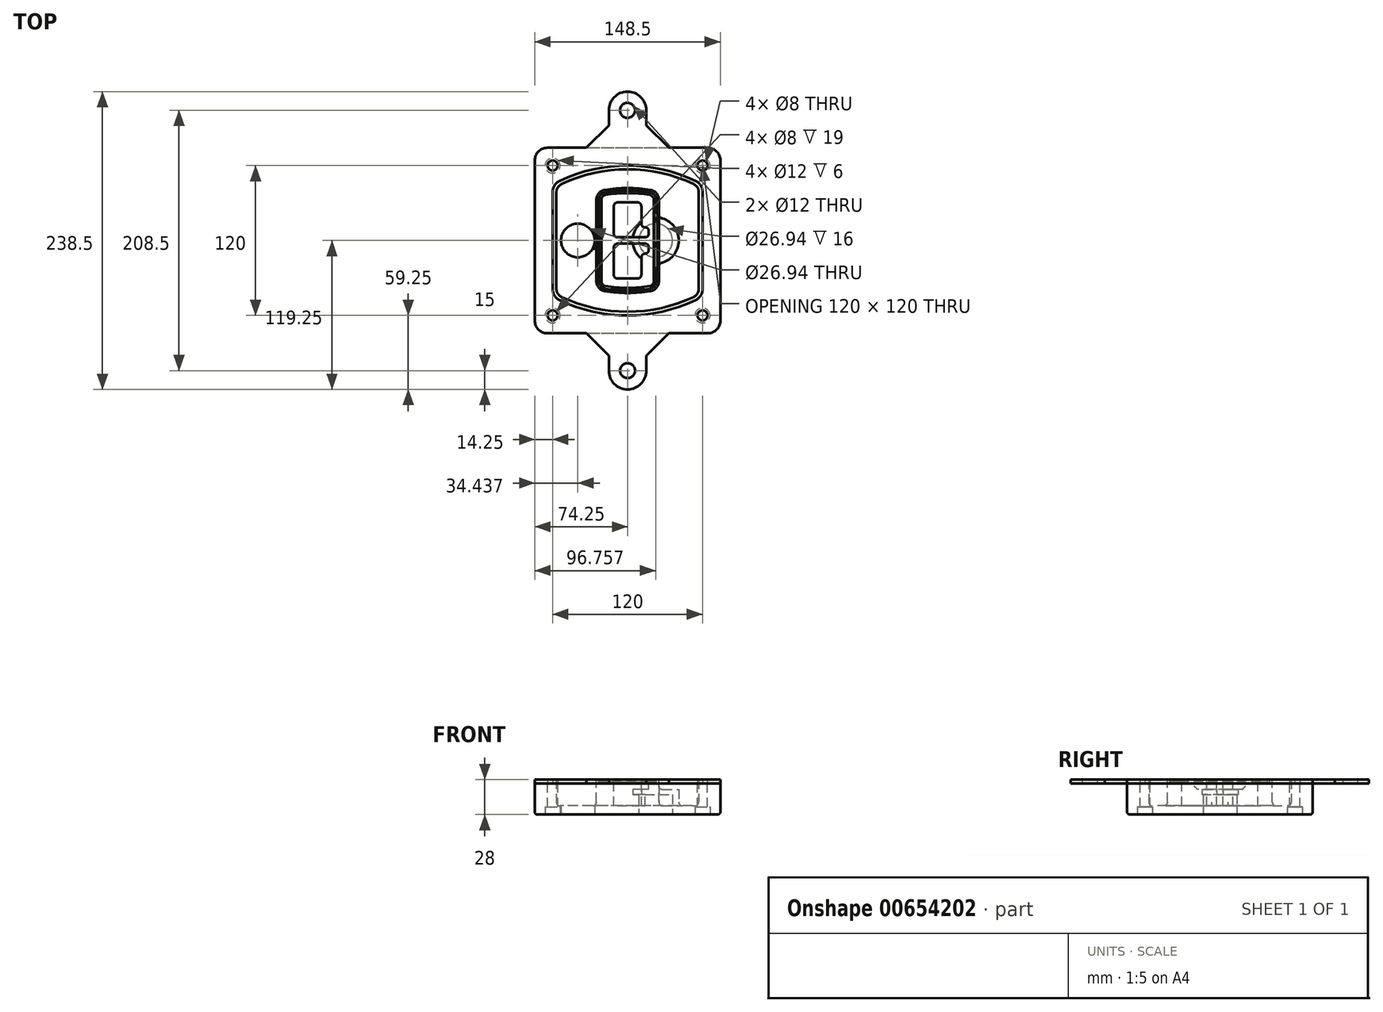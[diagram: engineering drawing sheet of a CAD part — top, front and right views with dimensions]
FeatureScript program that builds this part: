
annotation { "Feature Type Name" : "Feature", "Feature Type Description" : "" }
export const myFeature = defineFeature(function(context is Context, id is Id, definition is map)
    precondition{}
    {
        {
            var Q0;
            Q0=qCreatedBy(makeId("Top.planeOp"),FACE);
            var sketch = newSketch(context, id + "F0", { "sketchPlane" : qUnion([Q0])});
            skPoint(sketch, "E0.rect.middle", {"position": v(0, 0) * mm});
            skLineSegment(sketch, "E1.bottom", {"start": v(-64.25, -74.25) * mm, "end": v(64.25, -74.25) * mm});
            skLineSegment(sketch, "E1.top", {"start": v(-64.25, 74.25) * mm, "end": v(64.25, 74.25) * mm});
            skLineSegment(sketch, "E1.left", {"start": v(-74.25, -64.25) * mm, "end": v(-74.25, 64.25) * mm});
            skLineSegment(sketch, "E1.right", {"start": v(74.25, -64.25) * mm, "end": v(74.25, 64.25) * mm});
            skLineSegment(sketch, "E2", {"start": v(-74.25, 74.25) * mm, "end": v(74.25, -74.25) * mm, "construction": true});
            skLineSegment(sketch, "E3", {"start": v(74.25, 74.25) * mm, "end": v(-74.25, -74.25) * mm, "construction": true});
            skCircle(sketch, "E4", {"center": v(-60, 60) * mm, "radius": 4 * mm});
            skCircle(sketch, "E5", {"center": v(60, 60) * mm, "radius": 4 * mm});
            skCircle(sketch, "E6", {"center": v(60, -60) * mm, "radius": 4 * mm});
            skCircle(sketch, "E7", {"center": v(-60, -60) * mm, "radius": 4 * mm});
            skLineSegment(sketch, "E8", {"start": v(-60, 60) * mm, "end": v(60, 60) * mm, "construction": true});
            skLineSegment(sketch, "E9", {"start": v(60, 60) * mm, "end": v(60, -60) * mm, "construction": true});
            skLineSegment(sketch, "E10", {"start": v(60, -60) * mm, "end": v(-60, -60) * mm, "construction": true});
            skLineSegment(sketch, "E11", {"start": v(-60, -60) * mm, "end": v(-60, 60) * mm, "construction": true});
            skLineSegment(sketch, "E12", {"start": v(-60, 38.83) * mm, "end": v(-60, -38.83) * mm});
            skLineSegment(sketch, "E13", {"start": v(60, 38.83) * mm, "end": v(60, -38.83) * mm});
            skArc(sketch, "E14", {"start": v(54.26, 47.88) * mm, "mid": v(0, 60) * mm, "end": v(-54.26, 47.88) * mm});
            skArc(sketch, "E15", {"start": v(-54.26, -47.88) * mm, "mid": v(0, -60) * mm, "end": v(54.26, -47.88) * mm});
            skLineSegment(sketch, "E16", {"start": v(-60, 0) * mm, "end": v(60, 0) * mm, "construction": true});
            skPoint(sketch, "E17.visualSharp", {"position": v(-60, -45) * mm});
            skArc(sketch, "E17.filletArc", {"start": v(-60, -38.83) * mm, "mid": v(-58.44, -44.2) * mm, "end": v(-54.26, -47.88) * mm});
            skPoint(sketch, "E18.visualSharp", {"position": v(-60, 45) * mm});
            skArc(sketch, "E18.filletArc", {"start": v(-54.26, 47.88) * mm, "mid": v(-58.44, 44.2) * mm, "end": v(-60, 38.83) * mm});
            skPoint(sketch, "E19.visualSharp", {"position": v(60, 45) * mm});
            skArc(sketch, "E19.filletArc", {"start": v(60, 38.83) * mm, "mid": v(58.44, 44.2) * mm, "end": v(54.26, 47.88) * mm});
            skPoint(sketch, "E20.visualSharp", {"position": v(60, -45) * mm});
            skArc(sketch, "E20.filletArc", {"start": v(54.26, -47.88) * mm, "mid": v(58.44, -44.2) * mm, "end": v(60, -38.83) * mm});
            skPoint(sketch, "E21.visualSharp", {"position": v(-74.25, 74.25) * mm});
            skArc(sketch, "E21.filletArc", {"start": v(-64.25, 74.25) * mm, "mid": v(-71.32, 71.32) * mm, "end": v(-74.25, 64.25) * mm});
            skPoint(sketch, "E22.visualSharp", {"position": v(74.25, 74.25) * mm});
            skArc(sketch, "E22.filletArc", {"start": v(74.25, 64.25) * mm, "mid": v(71.32, 71.32) * mm, "end": v(64.25, 74.25) * mm});
            skPoint(sketch, "E23.visualSharp", {"position": v(74.25, -74.25) * mm});
            skArc(sketch, "E23.filletArc", {"start": v(64.25, -74.25) * mm, "mid": v(71.32, -71.32) * mm, "end": v(74.25, -64.25) * mm});
            skPoint(sketch, "E24.visualSharp", {"position": v(-74.25, -74.25) * mm});
            skArc(sketch, "E24.filletArc", {"start": v(-74.25, -64.25) * mm, "mid": v(-71.32, -71.32) * mm, "end": v(-64.25, -74.25) * mm});
            skArc(sketch, "E25.0", {"start": v(57, 38.83) * mm, "mid": v(55.9, 42.58) * mm, "end": v(52.98, 45.17) * mm});
            skLineSegment(sketch, "E25.1", {"start": v(57, 38.83) * mm, "end": v(57, -38.83) * mm});
            skArc(sketch, "E25.2", {"start": v(52.98, -45.17) * mm, "mid": v(55.9, -42.58) * mm, "end": v(57, -38.83) * mm});
            skArc(sketch, "E25.3", {"start": v(-52.98, -45.17) * mm, "mid": v(0, -57) * mm, "end": v(52.98, -45.17) * mm});
            skArc(sketch, "E25.4", {"start": v(-57, -38.83) * mm, "mid": v(-55.9, -42.58) * mm, "end": v(-52.98, -45.17) * mm});
            skArc(sketch, "E25.5", {"start": v(52.98, 45.17) * mm, "mid": v(0, 57) * mm, "end": v(-52.98, 45.17) * mm});
            skLineSegment(sketch, "E25.6", {"start": v(-57, 38.83) * mm, "end": v(-57, -38.83) * mm});
            skArc(sketch, "E25.7", {"start": v(-52.98, 45.17) * mm, "mid": v(-55.9, 42.58) * mm, "end": v(-57, 38.83) * mm});
            skArc(sketch, "E26.0", {"start": v(-55.96, 51.5) * mm, "mid": v(-61.82, 46.33) * mm, "end": v(-64, 38.83) * mm});
            skArc(sketch, "E26.1", {"start": v(55.96, 51.5) * mm, "mid": v(0, 64) * mm, "end": v(-55.96, 51.5) * mm});
            skArc(sketch, "E26.2", {"start": v(64, 38.83) * mm, "mid": v(61.82, 46.33) * mm, "end": v(55.96, 51.5) * mm});
            skLineSegment(sketch, "E26.3", {"start": v(64, 38.83) * mm, "end": v(64, -38.83) * mm});
            skArc(sketch, "E26.4", {"start": v(55.96, -51.5) * mm, "mid": v(61.82, -46.33) * mm, "end": v(64, -38.83) * mm});
            skLineSegment(sketch, "E26.5", {"start": v(-64, 38.83) * mm, "end": v(-64, -38.83) * mm});
            skArc(sketch, "E26.6", {"start": v(-55.96, -51.5) * mm, "mid": v(0, -64) * mm, "end": v(55.96, -51.5) * mm});
            skArc(sketch, "E26.7", {"start": v(-64, -38.83) * mm, "mid": v(-61.82, -46.33) * mm, "end": v(-55.96, -51.5) * mm});
            skSolve(sketch);
        }
        {
            var Q0;
            Q0=makeQuery(id+"F0.imprint","IMPRINT",FACE,{"disambiguationData":[TD([[makeQuery(id+"F0.imprint","IMPRINT",EDGE,{"derivedFrom":sQuery(id+"F0.wireOp",EDGE,"E1.bottom")}),1.0]])]});
            var Q1;
            Q1=makeQuery(id+"F0.imprint","IMPRINT",FACE,{"disambiguationData":[TD([[makeQuery(id+"F0.imprint","IMPRINT",EDGE,{"derivedFrom":sQuery(id+"F0.wireOp",EDGE,"E12")}),1.0]])]});
            var Q2;
            Q2=makeQuery(id+"F0.imprint","IMPRINT",FACE,{"disambiguationData":[TD([[makeQuery(id+"F0.imprint","IMPRINT",EDGE,{"derivedFrom":sQuery(id+"F0.wireOp",EDGE,"E25.0")}),1.0]])]});
            var Q3;
            Q3=makeQuery(id+"F0.imprint","IMPRINT",FACE,{"disambiguationData":[TD([[makeQuery(id+"F0.imprint","IMPRINT",EDGE,{"derivedFrom":sQuery(id+"F0.wireOp",EDGE,"E12")}),-1.0]])]});
            extrude(context, id + "F1", {"entities" : qUnion([Q0, Q1, Q2, Q3]), "oppositeDirection" : true, "depth" : 25 * mm});
        }
        {
            var Q0;
            Q0=makeQuery(id+"F0.imprint","IMPRINT",FACE,{"disambiguationData":[TD([[makeQuery(id+"F0.imprint","IMPRINT",EDGE,{"derivedFrom":sQuery(id+"F0.wireOp",EDGE,"E12")}),1.0]])]});
            extrude(context, id + "F2", {"entities" : qUnion([Q0]), "operationType" : NewBodyOperationType.ADD, "depth" : 3 * mm});
        }
        {
            var Q0;
            Q0=makeQuery(id+"F0.imprint","IMPRINT",FACE,{"disambiguationData":[TD([[makeQuery(id+"F0.imprint","IMPRINT",EDGE,{"derivedFrom":sQuery(id+"F0.wireOp",EDGE,"E25.0")}),1.0]])]});
            extrude(context, id + "F3", {"entities" : qUnion([Q0]), "operationType" : NewBodyOperationType.REMOVE, "oppositeDirection" : true, "depth" : 18 * mm});
        }
        {
            var Q0;
            Q0=makeQuery(id+"F2.opExtrude","CAP_FACE",FACE,{"disambiguationData":[OSD([sQuery(id+"F0.wireOp",EDGE,"E12"),sQuery(id+"F0.wireOp",EDGE,"E13"),sQuery(id+"F0.wireOp",EDGE,"E14"),sQuery(id+"F0.wireOp",EDGE,"E15"),sQuery(id+"F0.wireOp",EDGE,"E17.filletArc"),sQuery(id+"F0.wireOp",EDGE,"E18.filletArc"),sQuery(id+"F0.wireOp",EDGE,"E19.filletArc"),sQuery(id+"F0.wireOp",EDGE,"E20.filletArc"),sQuery(id+"F0.wireOp",EDGE,"E25.0"),sQuery(id+"F0.wireOp",EDGE,"E25.1"),sQuery(id+"F0.wireOp",EDGE,"E25.2"),sQuery(id+"F0.wireOp",EDGE,"E25.3"),sQuery(id+"F0.wireOp",EDGE,"E25.4"),sQuery(id+"F0.wireOp",EDGE,"E25.5"),sQuery(id+"F0.wireOp",EDGE,"E25.6"),sQuery(id+"F0.wireOp",EDGE,"E25.7")])],"isStart":false});
            var sketch = newSketch(context, id + "F4", { "sketchPlane" : qUnion([Q0])});
            skArc(sketch, "E27.0", {"start": v(-18.34, -40.45) * mm, "mid": v(0, -42) * mm, "end": v(18.34, -40.45) * mm});
            skArc(sketch, "E28.0", {"start": v(18.34, 40.45) * mm, "mid": v(0, 42) * mm, "end": v(-18.34, 40.45) * mm});
            skLineSegment(sketch, "E29", {"start": v(-25, 32.57) * mm, "end": v(-25, -32.57) * mm});
            skLineSegment(sketch, "E30", {"start": v(25, 32.57) * mm, "end": v(25, -32.57) * mm});
            skLineSegment(sketch, "E31", {"start": v(-25, 39.1) * mm, "end": v(25, 39.1) * mm, "construction": true});
            skLineSegment(sketch, "E32", {"start": v(-25, -39.1) * mm, "end": v(25, -39.1) * mm, "construction": true});
            skPoint(sketch, "E33.visualSharp", {"position": v(-25, 39.1) * mm});
            skArc(sketch, "E33.filletArc", {"start": v(-18.34, 40.45) * mm, "mid": v(-23.11, 37.73) * mm, "end": v(-25, 32.57) * mm});
            skPoint(sketch, "E34.visualSharp", {"position": v(25, 39.1) * mm});
            skArc(sketch, "E34.filletArc", {"start": v(25, 32.57) * mm, "mid": v(23.11, 37.73) * mm, "end": v(18.34, 40.45) * mm});
            skPoint(sketch, "E35.visualSharp", {"position": v(25, -39.1) * mm});
            skArc(sketch, "E35.filletArc", {"start": v(18.34, -40.45) * mm, "mid": v(23.11, -37.73) * mm, "end": v(25, -32.57) * mm});
            skPoint(sketch, "E36.visualSharp", {"position": v(-25, -39.1) * mm});
            skArc(sketch, "E36.filletArc", {"start": v(-25, -32.57) * mm, "mid": v(-23.11, -37.73) * mm, "end": v(-18.34, -40.45) * mm});
            skArc(sketch, "E37.0", {"start": v(52.98, 45.17) * mm, "mid": v(0, 57) * mm, "end": v(-52.98, 45.17) * mm});
            skArc(sketch, "E37.1", {"start": v(-52.98, 45.17) * mm, "mid": v(-55.9, 42.58) * mm, "end": v(-57, 38.83) * mm});
            skLineSegment(sketch, "E37.2", {"start": v(-57, 38.83) * mm, "end": v(-57, -38.83) * mm});
            skArc(sketch, "E37.3", {"start": v(-57, -38.83) * mm, "mid": v(-55.9, -42.58) * mm, "end": v(-52.98, -45.17) * mm});
            skArc(sketch, "E37.4", {"start": v(-52.98, -45.17) * mm, "mid": v(0, -57) * mm, "end": v(52.98, -45.17) * mm});
            skArc(sketch, "E37.5", {"start": v(52.98, -45.17) * mm, "mid": v(55.9, -42.58) * mm, "end": v(57, -38.83) * mm});
            skLineSegment(sketch, "E37.6", {"start": v(57, 38.83) * mm, "end": v(57, -38.83) * mm});
            skArc(sketch, "E37.7", {"start": v(57, 38.83) * mm, "mid": v(55.9, 42.58) * mm, "end": v(52.98, 45.17) * mm});
            skLineSegment(sketch, "E38.0", {"start": v(23, 32.57) * mm, "end": v(23, -32.57) * mm});
            skArc(sketch, "E38.1", {"start": v(18, -38.48) * mm, "mid": v(21.58, -36.44) * mm, "end": v(23, -32.57) * mm});
            skArc(sketch, "E38.2", {"start": v(-18, -38.48) * mm, "mid": v(0, -40) * mm, "end": v(18, -38.48) * mm});
            skArc(sketch, "E38.3", {"start": v(-23, -32.57) * mm, "mid": v(-21.58, -36.44) * mm, "end": v(-18, -38.48) * mm});
            skLineSegment(sketch, "E38.4", {"start": v(-23, 32.57) * mm, "end": v(-23, -32.57) * mm});
            skArc(sketch, "E38.5", {"start": v(23, 32.57) * mm, "mid": v(21.58, 36.44) * mm, "end": v(18, 38.48) * mm});
            skArc(sketch, "E38.6", {"start": v(-18, 38.48) * mm, "mid": v(-21.58, 36.44) * mm, "end": v(-23, 32.57) * mm});
            skArc(sketch, "E38.7", {"start": v(18, 38.48) * mm, "mid": v(0, 40) * mm, "end": v(-18, 38.48) * mm});
            skArc(sketch, "E39.0", {"start": v(21, 32.57) * mm, "mid": v(20.06, 35.15) * mm, "end": v(17.67, 36.5) * mm});
            skLineSegment(sketch, "E39.1", {"start": v(21, 32.57) * mm, "end": v(21, -32.57) * mm});
            skArc(sketch, "E39.2", {"start": v(17.67, -36.5) * mm, "mid": v(20.06, -35.15) * mm, "end": v(21, -32.57) * mm});
            skArc(sketch, "E39.3", {"start": v(-17.67, -36.5) * mm, "mid": v(0, -38) * mm, "end": v(17.67, -36.5) * mm});
            skArc(sketch, "E39.4", {"start": v(-21, -32.57) * mm, "mid": v(-20.06, -35.15) * mm, "end": v(-17.67, -36.5) * mm});
            skArc(sketch, "E39.5", {"start": v(17.67, 36.5) * mm, "mid": v(0, 38) * mm, "end": v(-17.67, 36.5) * mm});
            skLineSegment(sketch, "E39.6", {"start": v(-21, 32.57) * mm, "end": v(-21, -32.57) * mm});
            skArc(sketch, "E39.7", {"start": v(-17.67, 36.5) * mm, "mid": v(-20.06, 35.15) * mm, "end": v(-21, 32.57) * mm});
            skLineSegment(sketch, "E40", {"start": v(-25, 0) * mm, "end": v(25, 0) * mm, "construction": true});
            skLineSegment(sketch, "E41", {"start": v(-11, 5.5) * mm, "end": v(-11, 27.5) * mm});
            skLineSegment(sketch, "E42", {"start": v(-8, 30.5) * mm, "end": v(8, 30.5) * mm});
            skLineSegment(sketch, "E43", {"start": v(11, 27.5) * mm, "end": v(11, 13.5) * mm});
            skLineSegment(sketch, "E44", {"start": v(14, 10.5) * mm, "end": v(14, 10.5) * mm});
            skLineSegment(sketch, "E45", {"start": v(17, 7.5) * mm, "end": v(17, 5.5) * mm});
            skLineSegment(sketch, "E46", {"start": v(14, 2.5) * mm, "end": v(-8, 2.5) * mm});
            skPoint(sketch, "E47.visualSharp", {"position": v(-11, 30.5) * mm});
            skArc(sketch, "E47.filletArc", {"start": v(-8, 30.5) * mm, "mid": v(-10.12, 29.62) * mm, "end": v(-11, 27.5) * mm});
            skPoint(sketch, "E48.visualSharp", {"position": v(11, 30.5) * mm});
            skArc(sketch, "E48.filletArc", {"start": v(11, 27.5) * mm, "mid": v(10.12, 29.62) * mm, "end": v(8, 30.5) * mm});
            skPoint(sketch, "E49.visualSharp", {"position": v(11, 10.5) * mm});
            skArc(sketch, "E49.filletArc", {"start": v(11, 13.5) * mm, "mid": v(11.88, 11.38) * mm, "end": v(14, 10.5) * mm});
            skPoint(sketch, "E50.visualSharp", {"position": v(17, 10.5) * mm});
            skArc(sketch, "E50.filletArc", {"start": v(17, 7.5) * mm, "mid": v(16.12, 9.62) * mm, "end": v(14, 10.5) * mm});
            skPoint(sketch, "E51.visualSharp", {"position": v(17, 2.5) * mm});
            skArc(sketch, "E51.filletArc", {"start": v(14, 2.5) * mm, "mid": v(16.12, 3.38) * mm, "end": v(17, 5.5) * mm});
            skPoint(sketch, "E52.visualSharp", {"position": v(-11, 2.5) * mm});
            skArc(sketch, "E52.filletArc", {"start": v(-11, 5.5) * mm, "mid": v(-10.12, 3.38) * mm, "end": v(-8, 2.5) * mm});
            skLineSegment(sketch, "E53.0.MirrorCS", {"start": v(14, -2.5) * mm, "end": v(-8, -2.5) * mm});
            skArc(sketch, "E54.0.MirrorCS", {"start": v(-11, -5.5) * mm, "mid": v(-10.12, -3.38) * mm, "end": v(-8, -2.5) * mm});
            skLineSegment(sketch, "E55.0.MirrorCS", {"start": v(-11, -5.5) * mm, "end": v(-11, -27.5) * mm});
            skArc(sketch, "E56.0.MirrorCS", {"start": v(-8, -30.5) * mm, "mid": v(-10.12, -29.62) * mm, "end": v(-11, -27.5) * mm});
            skLineSegment(sketch, "E57.0.MirrorCS", {"start": v(-8, -30.5) * mm, "end": v(8, -30.5) * mm});
            skArc(sketch, "E58.0.MirrorCS", {"start": v(11, -27.5) * mm, "mid": v(10.12, -29.62) * mm, "end": v(8, -30.5) * mm});
            skLineSegment(sketch, "E59.0.MirrorCS", {"start": v(11, -27.5) * mm, "end": v(11, -13.5) * mm});
            skArc(sketch, "E60.0.MirrorCS", {"start": v(11, -13.5) * mm, "mid": v(11.88, -11.38) * mm, "end": v(14, -10.5) * mm});
            skArc(sketch, "E61.0.MirrorCS", {"start": v(17, -7.5) * mm, "mid": v(16.12, -9.62) * mm, "end": v(14, -10.5) * mm});
            skLineSegment(sketch, "E62.0.MirrorCS", {"start": v(17, -7.5) * mm, "end": v(17, -5.5) * mm});
            skArc(sketch, "E63.0.MirrorCS", {"start": v(14, -2.5) * mm, "mid": v(16.12, -3.38) * mm, "end": v(17, -5.5) * mm});
            skSolve(sketch);
        }
        {
            var Q0;
            Q0=makeQuery(id+"F4.imprint","IMPRINT",FACE,{"disambiguationData":[TD([[makeQuery(id+"F4.imprint","IMPRINT",EDGE,{"derivedFrom":sQuery(id+"F4.wireOp",EDGE,"E27.0")}),1.0]])]});
            var Q1;
            Q1=makeQuery(id+"F4.imprint","IMPRINT",FACE,{"disambiguationData":[TD([[makeQuery(id+"F4.imprint","IMPRINT",EDGE,{"derivedFrom":sQuery(id+"F4.wireOp",EDGE,"E38.0")}),-1.0]])]});
            var Q2;
            Q2=makeQuery(id+"F4.imprint","IMPRINT",FACE,{"disambiguationData":[TD([[makeQuery(id+"F4.imprint","IMPRINT",EDGE,{"derivedFrom":sQuery(id+"F4.wireOp",EDGE,"E39.0")}),1.0]])]});
            extrude(context, id + "F5", {"entities" : qUnion([Q0, Q1, Q2]), "operationType" : NewBodyOperationType.ADD, "endBound" : BoundingType.UP_TO_NEXT, "oppositeDirection" : true, "depth" : 25 * mm});
        }
        {
            var Q0;
            Q0=makeQuery(id+"F4.imprint","IMPRINT",FACE,{"disambiguationData":[TD([[makeQuery(id+"F4.imprint","IMPRINT",EDGE,{"derivedFrom":sQuery(id+"F4.wireOp",EDGE,"E38.0")}),-1.0]])]});
            extrude(context, id + "F6", {"entities" : qUnion([Q0]), "operationType" : NewBodyOperationType.REMOVE, "oppositeDirection" : true, "depth" : 2 * mm});
        }
        {
            var Q0;
            Q0=makeQuery(id+"F1.opExtrude","CAP_FACE",FACE,{"disambiguationData":[OSD([sQuery(id+"F0.wireOp",EDGE,"E1.bottom"),sQuery(id+"F0.wireOp",EDGE,"E1.top"),sQuery(id+"F0.wireOp",EDGE,"E1.left"),sQuery(id+"F0.wireOp",EDGE,"E1.right"),sQuery(id+"F0.wireOp",EDGE,"E4"),sQuery(id+"F0.wireOp",EDGE,"E5"),sQuery(id+"F0.wireOp",EDGE,"E6"),sQuery(id+"F0.wireOp",EDGE,"E7"),sQuery(id+"F0.wireOp",EDGE,"E21.filletArc"),sQuery(id+"F0.wireOp",EDGE,"E22.filletArc"),sQuery(id+"F0.wireOp",EDGE,"E23.filletArc"),sQuery(id+"F0.wireOp",EDGE,"E24.filletArc")])],"isStart":false});
            var sketch = newSketch(context, id + "F7", { "sketchPlane" : qUnion([Q0])});
            skCircle(sketch, "E64", {"center": v(22.5, 0) * mm, "radius": 13.47 * mm});
            skCircle(sketch, "E65", {"center": v(-39.81, 0) * mm, "radius": 13.47 * mm});
            skLineSegment(sketch, "E66", {"start": v(74.25, 0) * mm, "end": v(-74.25, 0) * mm});
            skCircle(sketch, "E67", {"center": v(22.5, 0) * mm, "radius": 18.47 * mm});
            skCircle(sketch, "E68", {"center": v(60, -60) * mm, "radius": 6 * mm});
            skCircle(sketch, "E69", {"center": v(-60, -60) * mm, "radius": 6 * mm});
            skCircle(sketch, "E70", {"center": v(-60, 60) * mm, "radius": 6 * mm});
            skCircle(sketch, "E71", {"center": v(60, 60) * mm, "radius": 6 * mm});
            skSolve(sketch);
        }
        {
            var Q0;
            {var subQ1=sQuery(id+"F7.wireOp",EDGE,"E66");var subQ4=sQuery(id+"F7.wireOp",EDGE,"E64");var subQ6=makeQuery(id+"F7.imprint","INTERSECT",VERTEX,{"disambiguationData":[OD(0.0)],"derivedFrom":[subQ4,subQ1]});Q0=makeQuery(id+"F7.imprint","IMPRINT",FACE,{"disambiguationData":[TD([[makeQuery(id+"F7.imprint","IMPRINT",EDGE,{"disambiguationData":[TD([[subQ6,-1.0]])],"derivedFrom":subQ4}),-1.0]])]});}
            var Q1;
            {var subQ0=sQuery(id+"F7.wireOp",EDGE,"E66");var subQ1=sQuery(id+"F7.wireOp",EDGE,"E64");var subQ3=makeQuery(id+"F7.imprint","INTERSECT",VERTEX,{"disambiguationData":[OD(0.0)],"derivedFrom":[subQ1,subQ0]});Q1=makeQuery(id+"F7.imprint","IMPRINT",FACE,{"disambiguationData":[TD([[makeQuery(id+"F7.imprint","IMPRINT",EDGE,{"disambiguationData":[TD([[subQ3,-1.0]])],"derivedFrom":subQ1}),1.0]])]});}
            var Q2;
            {var subQ0=sQuery(id+"F7.wireOp",EDGE,"E66");var subQ1=sQuery(id+"F7.wireOp",EDGE,"E64");var subQ3=makeQuery(id+"F7.imprint","INTERSECT",VERTEX,{"disambiguationData":[OD(0.0)],"derivedFrom":[subQ1,subQ0]});Q2=makeQuery(id+"F7.imprint","IMPRINT",FACE,{"disambiguationData":[TD([[makeQuery(id+"F7.imprint","IMPRINT",EDGE,{"disambiguationData":[TD([[subQ3,1.0]])],"derivedFrom":subQ1}),1.0]])]});}
            var Q3;
            {var subQ1=sQuery(id+"F7.wireOp",EDGE,"E66");var subQ4=sQuery(id+"F7.wireOp",EDGE,"E64");var subQ6=makeQuery(id+"F7.imprint","INTERSECT",VERTEX,{"disambiguationData":[OD(0.0)],"derivedFrom":[subQ4,subQ1]});Q3=makeQuery(id+"F7.imprint","IMPRINT",FACE,{"disambiguationData":[TD([[makeQuery(id+"F7.imprint","IMPRINT",EDGE,{"disambiguationData":[TD([[subQ6,1.0]])],"derivedFrom":subQ4}),-1.0]])]});}
            extrude(context, id + "F8", {"entities" : qUnion([Q0, Q1, Q2, Q3]), "operationType" : NewBodyOperationType.ADD, "oppositeDirection" : true, "depth" : 20 * mm});
        }
        {
            var Q0;
            {var subQ0=sQuery(id+"F7.wireOp",EDGE,"E66");var subQ1=sQuery(id+"F7.wireOp",EDGE,"E64");var subQ3=makeQuery(id+"F7.imprint","INTERSECT",VERTEX,{"disambiguationData":[OD(0.0)],"derivedFrom":[subQ1,subQ0]});Q0=makeQuery(id+"F7.imprint","IMPRINT",FACE,{"disambiguationData":[TD([[makeQuery(id+"F7.imprint","IMPRINT",EDGE,{"disambiguationData":[TD([[subQ3,-1.0]])],"derivedFrom":subQ1}),1.0]])]});}
            var Q1;
            {var subQ0=sQuery(id+"F7.wireOp",EDGE,"E66");var subQ1=sQuery(id+"F7.wireOp",EDGE,"E64");var subQ3=makeQuery(id+"F7.imprint","INTERSECT",VERTEX,{"disambiguationData":[OD(0.0)],"derivedFrom":[subQ1,subQ0]});Q1=makeQuery(id+"F7.imprint","IMPRINT",FACE,{"disambiguationData":[TD([[makeQuery(id+"F7.imprint","IMPRINT",EDGE,{"disambiguationData":[TD([[subQ3,1.0]])],"derivedFrom":subQ1}),1.0]])]});}
            extrude(context, id + "F9", {"entities" : qUnion([Q0, Q1]), "operationType" : NewBodyOperationType.REMOVE, "oppositeDirection" : true, "depth" : 16 * mm});
        }
        {
            var Q0;
            {var subQ0=sQuery(id+"F7.wireOp",EDGE,"E66");var subQ1=sQuery(id+"F7.wireOp",EDGE,"E65");var subQ3=makeQuery(id+"F7.imprint","INTERSECT",VERTEX,{"disambiguationData":[OD(0.0)],"derivedFrom":[subQ1,subQ0]});Q0=makeQuery(id+"F7.imprint","IMPRINT",FACE,{"disambiguationData":[TD([[makeQuery(id+"F7.imprint","IMPRINT",EDGE,{"disambiguationData":[TD([[subQ3,-1.0]])],"derivedFrom":subQ1}),1.0]])]});}
            var Q1;
            {var subQ0=sQuery(id+"F7.wireOp",EDGE,"E66");var subQ1=sQuery(id+"F7.wireOp",EDGE,"E65");var subQ3=makeQuery(id+"F7.imprint","INTERSECT",VERTEX,{"disambiguationData":[OD(0.0)],"derivedFrom":[subQ1,subQ0]});Q1=makeQuery(id+"F7.imprint","IMPRINT",FACE,{"disambiguationData":[TD([[makeQuery(id+"F7.imprint","IMPRINT",EDGE,{"disambiguationData":[TD([[subQ3,1.0]])],"derivedFrom":subQ1}),1.0]])]});}
            extrude(context, id + "F10", {"entities" : qUnion([Q0, Q1]), "operationType" : NewBodyOperationType.REMOVE, "oppositeDirection" : true, "depth" : 25 * mm});
        }
        {
            var Q0;
            Q0=makeQuery(id+"F7.imprint","IMPRINT",FACE,{"disambiguationData":[TD([[makeQuery(id+"F7.imprint","IMPRINT",EDGE,{"derivedFrom":sQuery(id+"F7.wireOp",EDGE,"E68")}),1.0]])]});
            var Q1;
            Q1=makeQuery(id+"F7.imprint","IMPRINT",FACE,{"disambiguationData":[TD([[makeQuery(id+"F7.imprint","IMPRINT",EDGE,{"derivedFrom":makeQuery(id+"F1.opExtrude","CAP_EDGE",EDGE,{"disambiguationData":[OSD([sQuery(id+"F0.wireOp",EDGE,"E5")])],"isStart":false})}),-1.0]])]});
            var Q2;
            Q2=makeQuery(id+"F7.imprint","IMPRINT",FACE,{"disambiguationData":[TD([[makeQuery(id+"F7.imprint","IMPRINT",EDGE,{"derivedFrom":sQuery(id+"F7.wireOp",EDGE,"E69")}),1.0]])]});
            var Q3;
            Q3=makeQuery(id+"F7.imprint","IMPRINT",FACE,{"disambiguationData":[TD([[makeQuery(id+"F7.imprint","IMPRINT",EDGE,{"derivedFrom":makeQuery(id+"F1.opExtrude","CAP_EDGE",EDGE,{"disambiguationData":[OSD([sQuery(id+"F0.wireOp",EDGE,"E4")])],"isStart":false})}),-1.0]])]});
            var Q4;
            Q4=makeQuery(id+"F7.imprint","IMPRINT",FACE,{"disambiguationData":[TD([[makeQuery(id+"F7.imprint","IMPRINT",EDGE,{"derivedFrom":sQuery(id+"F7.wireOp",EDGE,"E70")}),1.0]])]});
            var Q5;
            Q5=makeQuery(id+"F7.imprint","IMPRINT",FACE,{"disambiguationData":[TD([[makeQuery(id+"F7.imprint","IMPRINT",EDGE,{"derivedFrom":makeQuery(id+"F1.opExtrude","CAP_EDGE",EDGE,{"disambiguationData":[OSD([sQuery(id+"F0.wireOp",EDGE,"E7")])],"isStart":false})}),-1.0]])]});
            var Q6;
            Q6=makeQuery(id+"F7.imprint","IMPRINT",FACE,{"disambiguationData":[TD([[makeQuery(id+"F7.imprint","IMPRINT",EDGE,{"derivedFrom":sQuery(id+"F7.wireOp",EDGE,"E71")}),1.0]])]});
            var Q7;
            Q7=makeQuery(id+"F7.imprint","IMPRINT",FACE,{"disambiguationData":[TD([[makeQuery(id+"F7.imprint","IMPRINT",EDGE,{"derivedFrom":makeQuery(id+"F1.opExtrude","CAP_EDGE",EDGE,{"disambiguationData":[OSD([sQuery(id+"F0.wireOp",EDGE,"E6")])],"isStart":false})}),-1.0]])]});
            extrude(context, id + "F11", {"entities" : qUnion([Q0, Q1, Q2, Q3, Q4, Q5, Q6, Q7]), "operationType" : NewBodyOperationType.REMOVE, "oppositeDirection" : true, "depth" : 6 * mm});
        }
        {
            var Q0;
            Q0=makeQuery(id+"F9.boolean.opBoolean","COPY",FACE,{"derivedFrom":makeQuery(id+"F9.opExtrude","CAP_FACE",FACE,{"disambiguationData":[OSD([sQuery(id+"F7.wireOp",EDGE,"E64")])],"isStart":false})});
            var sketch = newSketch(context, id + "F12", { "sketchPlane" : qUnion([Q0])});
            skArc(sketch, "E72.0", {"start": v(11, 14.45) * mm, "mid": v(6.45, 9.13) * mm, "end": v(4.2, 2.5) * mm});
            skArc(sketch, "E72.1", {"start": v(4.2, -2.5) * mm, "mid": v(6.45, -9.13) * mm, "end": v(11, -14.45) * mm});
            skLineSegment(sketch, "E73", {"start": v(4.2, -2.5) * mm, "end": v(14, -2.5) * mm});
            skLineSegment(sketch, "E74.0", {"start": v(14, 2.5) * mm, "end": v(4.2, 2.5) * mm});
            skArc(sketch, "E74.1", {"start": v(14, 2.5) * mm, "mid": v(16.12, 3.38) * mm, "end": v(17, 5.5) * mm});
            skLineSegment(sketch, "E74.2", {"start": v(17, 7.5) * mm, "end": v(17, 5.5) * mm});
            skArc(sketch, "E74.3", {"start": v(17, 7.5) * mm, "mid": v(16.12, 9.62) * mm, "end": v(14, 10.5) * mm});
            skArc(sketch, "E74.4", {"start": v(11, 13.5) * mm, "mid": v(11.88, 11.38) * mm, "end": v(14, 10.5) * mm});
            skLineSegment(sketch, "E74.5", {"start": v(11, 14.45) * mm, "end": v(11, 13.5) * mm});
            skLineSegment(sketch, "E74.7", {"start": v(14, -2.5) * mm, "end": v(4.2, -2.5) * mm});
            skArc(sketch, "E74.8", {"start": v(14, -2.5) * mm, "mid": v(16.12, -3.38) * mm, "end": v(17, -5.5) * mm});
            skLineSegment(sketch, "E74.9", {"start": v(17, -7.5) * mm, "end": v(17, -5.5) * mm});
            skArc(sketch, "E74.10", {"start": v(17, -7.5) * mm, "mid": v(16.12, -9.62) * mm, "end": v(14, -10.5) * mm});
            skArc(sketch, "E74.11", {"start": v(11, -13.5) * mm, "mid": v(11.88, -11.38) * mm, "end": v(14, -10.5) * mm});
            skLineSegment(sketch, "E74.12", {"start": v(11, -14.45) * mm, "end": v(11, -13.5) * mm});
            skPoint(sketch, "E75.orphan", {"position": v(11, -27.5) * mm});
            skPoint(sketch, "E76.orphan", {"position": v(-8, -2.5) * mm});
            skPoint(sketch, "E77.orphan", {"position": v(-8, 2.5) * mm});
            skPoint(sketch, "E78.orphan", {"position": v(11, 27.5) * mm});
            skSolve(sketch);
        }
        {
            var Q0;
            {var subQ7=sQuery(id+"F12.wireOp",EDGE,"E72.0");var subQ14=sQuery(id+"F12.wireOp",EDGE,"E72.1");var subQ16=sQuery(id+"F12.wireOp",EDGE,"E74.1");var subQ18=sQuery(id+"F12.wireOp",EDGE,"E74.8");Q0=qUnion([makeQuery(id+"F12.imprint","IMPRINT",FACE,{"disambiguationData":[TD([[makeQuery(id+"F12.imprint","IMPRINT",EDGE,{"derivedFrom":subQ7}),1.0]])]}),makeQuery(id+"F12.imprint","IMPRINT",FACE,{"disambiguationData":[TD([[makeQuery(id+"F12.imprint","IMPRINT",EDGE,{"derivedFrom":subQ14}),1.0]])]}),makeQuery(id+"F12.imprint","IMPRINT",FACE,{"disambiguationData":[TD([[makeQuery(id+"F12.imprint","IMPRINT",EDGE,{"derivedFrom":subQ16}),1.0]])]}),makeQuery(id+"F12.imprint","IMPRINT",FACE,{"disambiguationData":[TD([[makeQuery(id+"F12.imprint","IMPRINT",EDGE,{"derivedFrom":subQ18}),-1.0]])]})]);}
            var Q1;
            Q1=makeQuery(id+"F5.boolean.opBoolean","SPLIT",FACE,{"disambiguationData":[TD([makeQuery(id+"F5.opExtrude","SWEPT_FACE",FACE,{"disambiguationData":[OSD([sQuery(id+"F4.wireOp",EDGE,"E41")])]})])],"derivedFrom":makeQuery(id+"F3.boolean.opBoolean","COPY",FACE,{"derivedFrom":makeQuery(id+"F3.opExtrude","CAP_FACE",FACE,{"disambiguationData":[OSD([sQuery(id+"F0.wireOp",EDGE,"E25.0"),sQuery(id+"F0.wireOp",EDGE,"E25.1"),sQuery(id+"F0.wireOp",EDGE,"E25.2"),sQuery(id+"F0.wireOp",EDGE,"E25.3"),sQuery(id+"F0.wireOp",EDGE,"E25.4"),sQuery(id+"F0.wireOp",EDGE,"E25.5"),sQuery(id+"F0.wireOp",EDGE,"E25.6"),sQuery(id+"F0.wireOp",EDGE,"E25.7")])],"isStart":false})})});
            extrude(context, id + "F13", {"entities" : qUnion([Q0]), "operationType" : NewBodyOperationType.REMOVE, "endBound" : BoundingType.UP_TO_SURFACE, "endBoundEntityFace" : qUnion([Q1]), "depth" : 25 * mm});
        }
        {
            var Q0;
            Q0=makeQuery(id+"F3.boolean.opBoolean","COPY",EDGE,{"derivedFrom":makeQuery(id+"F3.opExtrude","CAP_EDGE",EDGE,{"disambiguationData":[OSD([sQuery(id+"F0.wireOp",EDGE,"E25.6")])],"isStart":false})});
            var Q1;
            Q1=makeQuery(id+"F8.boolean.opBoolean","INTERSECT",EDGE,{"derivedFrom":[makeQuery(id+"F5.opExtrude","SWEPT_FACE",FACE,{"disambiguationData":[OSD([sQuery(id+"F4.wireOp",EDGE,"E30")])]}),makeQuery(id+"F8.opExtrude","CAP_FACE",FACE,{"disambiguationData":[OSD([sQuery(id+"F7.wireOp",EDGE,"E67")])],"isStart":false})]});
            var Q2;
            Q2=makeQuery(id+"F8.boolean.opBoolean","INTERSECT",EDGE,{"disambiguationData":[OD(1.0)],"derivedFrom":[makeQuery(id+"F5.opExtrude","SWEPT_FACE",FACE,{"disambiguationData":[OSD([sQuery(id+"F4.wireOp",EDGE,"E30")])]}),makeQuery(id+"F8.opExtrude","SWEPT_FACE",FACE,{"disambiguationData":[OSD([sQuery(id+"F7.wireOp",EDGE,"E67")])]})]});
            var Q3;
            {var subQ0=sQuery(id+"F4.wireOp",EDGE,"E30");Q3=makeQuery(id+"F8.boolean.opBoolean","SPLIT",EDGE,{"disambiguationData":[TD([makeQuery(id+"F5.opExtrude","SWEPT_FACE",FACE,{"disambiguationData":[OSD([sQuery(id+"F4.wireOp",EDGE,"E35.filletArc")])]})])],"derivedFrom":makeQuery(id+"F5.opExtrude","CAP_EDGE",EDGE,{"disambiguationData":[OSD([subQ0])],"isStart":false})});}
            var Q4;
            {var subQ0=sQuery(id+"F0.wireOp",EDGE,"E25.7");var subQ1=sQuery(id+"F0.wireOp",EDGE,"E25.1");var subQ2=sQuery(id+"F0.wireOp",EDGE,"E25.6");var subQ3=sQuery(id+"F0.wireOp",EDGE,"E25.5");var subQ4=sQuery(id+"F0.wireOp",EDGE,"E25.4");var subQ5=sQuery(id+"F0.wireOp",EDGE,"E25.0");var subQ6=sQuery(id+"F0.wireOp",EDGE,"E25.2");var subQ7=sQuery(id+"F0.wireOp",EDGE,"E25.3");Q4=makeQuery(id+"F8.boolean.opBoolean","INTERSECT",EDGE,{"derivedFrom":[makeQuery(id+"F5.boolean.opBoolean","SPLIT",FACE,{"disambiguationData":[TD([makeQuery(id+"F2.opExtrude","SWEPT_FACE",FACE,{"disambiguationData":[OSD([subQ5])]})])],"derivedFrom":makeQuery(id+"F3.boolean.opBoolean","COPY",FACE,{"derivedFrom":makeQuery(id+"F3.opExtrude","CAP_FACE",FACE,{"disambiguationData":[OSD([subQ5,subQ1,subQ6,subQ7,subQ4,subQ3,subQ2,subQ0])],"isStart":false})})}),makeQuery(id+"F8.opExtrude","SWEPT_FACE",FACE,{"disambiguationData":[OSD([sQuery(id+"F7.wireOp",EDGE,"E67")])]})]});}
            var Q5;
            Q5=makeQuery(id+"F8.boolean.opBoolean","INTERSECT",EDGE,{"disambiguationData":[OD(0.0)],"derivedFrom":[makeQuery(id+"F5.opExtrude","SWEPT_FACE",FACE,{"disambiguationData":[OSD([sQuery(id+"F4.wireOp",EDGE,"E30")])]}),makeQuery(id+"F8.opExtrude","SWEPT_FACE",FACE,{"disambiguationData":[OSD([sQuery(id+"F7.wireOp",EDGE,"E67")])]})]});
            fillet(context, id + "F14", {"entities" : qUnion([Q0, Q1, Q2, Q3, Q4, Q5]), "radius" : 3 * mm, "tangentPropagation" : true, "allowEdgeOverflow" : false});
        }
        {
            var Q0;
            Q0=makeQuery(id+"F1.opExtrude","CAP_EDGE",EDGE,{"disambiguationData":[OSD([sQuery(id+"F0.wireOp",EDGE,"E1.bottom")])],"isStart":false});
            fillet(context, id + "F15", {"entities" : qUnion([Q0]), "radius" : 2 * mm, "tangentPropagation" : true, "allowEdgeOverflow" : false});
        }
        {
            var Q0;
            {var subQ0=sQuery(id+"F0.wireOp",EDGE,"E21.filletArc");var subQ1=sQuery(id+"F0.wireOp",EDGE,"E7");var subQ2=sQuery(id+"F0.wireOp",EDGE,"E6");var subQ3=sQuery(id+"F0.wireOp",EDGE,"E5");var subQ4=sQuery(id+"F0.wireOp",EDGE,"E4");var subQ5=sQuery(id+"F0.wireOp",EDGE,"E22.filletArc");var subQ6=sQuery(id+"F0.wireOp",EDGE,"E1.bottom");var subQ7=sQuery(id+"F0.wireOp",EDGE,"E1.right");var subQ8=sQuery(id+"F0.wireOp",EDGE,"E1.top");var subQ9=sQuery(id+"F0.wireOp",EDGE,"E1.left");var subQ10=sQuery(id+"F0.wireOp",EDGE,"E23.filletArc");var subQ11=sQuery(id+"F0.wireOp",EDGE,"E24.filletArc");Q0=makeQuery(id+"F2.boolean.opBoolean","SPLIT",FACE,{"disambiguationData":[TD([makeQuery(id+"F1.opExtrude","SWEPT_FACE",FACE,{"disambiguationData":[OSD([subQ6])]})])],"derivedFrom":makeQuery(id+"F1.opExtrude","CAP_FACE",FACE,{"disambiguationData":[OSD([subQ6,subQ8,subQ9,subQ7,subQ4,subQ3,subQ2,subQ1,subQ0,subQ5,subQ10,subQ11])],"isStart":true})});}
            var sketch = newSketch(context, id + "F16", { "sketchPlane" : qUnion([Q0])});
            skLineSegment(sketch, "E79", {"start": v(-32.83, 74.25) * mm, "end": v(-32.83, 74.25) * mm});
            skLineSegment(sketch, "E80", {"start": v(15, 92.16) * mm, "end": v(15, 104.25) * mm});
            skLineSegment(sketch, "E81", {"start": v(-32.83, 74.25) * mm, "end": v(-15, 92.25) * mm});
            skLineSegment(sketch, "E82", {"start": v(-15, 92.25) * mm, "end": v(-15, 104.25) * mm});
            skArc(sketch, "E83", {"start": v(15, 104.25) * mm, "mid": v(0, 119.25) * mm, "end": v(-15, 104.25) * mm});
            skCircle(sketch, "E84", {"center": v(0, 104.25) * mm, "radius": 6 * mm});
            skLineSegment(sketch, "E85", {"start": v(0, 104.25) * mm, "end": v(0, 60) * mm, "construction": true});
            skLineSegment(sketch, "E86", {"start": v(-32.83, 74.25) * mm, "end": v(32.91, 74.25) * mm});
            skLineSegment(sketch, "E87", {"start": v(32.91, 74.25) * mm, "end": v(15, 92.16) * mm});
            skLineSegment(sketch, "E88", {"start": v(-74.25, 0) * mm, "end": v(74.25, 0) * mm, "construction": true});
            skLineSegment(sketch, "E89.MirrorCS", {"start": v(32.91, -74.25) * mm, "end": v(15, -92.16) * mm});
            skLineSegment(sketch, "E90.MirrorCS", {"start": v(15, -92.16) * mm, "end": v(15, -104.25) * mm});
            skArc(sketch, "E91.MirrorCS", {"start": v(15, -104.25) * mm, "mid": v(0, -119.25) * mm, "end": v(-15, -104.25) * mm});
            skLineSegment(sketch, "E92.MirrorCS", {"start": v(-15, -92.25) * mm, "end": v(-15, -104.25) * mm});
            skCircle(sketch, "E93.MirrorC", {"center": v(0, -104.25) * mm, "radius": 6 * mm});
            skLineSegment(sketch, "E94.MirrorCS", {"start": v(0, -104.25) * mm, "end": v(0, -60) * mm, "construction": true});
            skLineSegment(sketch, "E95.MirrorCS", {"start": v(-32.83, -74.25) * mm, "end": v(-15, -92.25) * mm});
            skLineSegment(sketch, "E96.MirrorCS", {"start": v(-32.83, -74.25) * mm, "end": v(32.91, -74.25) * mm});
            skSolve(sketch);
        }
        {
            var Q0;
            Q0=makeQuery(id+"F16.imprint","IMPRINT",FACE,{"disambiguationData":[TD([[makeQuery(id+"F16.imprint","IMPRINT",EDGE,{"derivedFrom":sQuery(id+"F16.wireOp",EDGE,"E80")}),1.0]])]});
            var Q1;
            Q1=makeQuery(id+"F16.imprint","IMPRINT",FACE,{"disambiguationData":[TD([[makeQuery(id+"F16.imprint","IMPRINT",EDGE,{"derivedFrom":sQuery(id+"F16.wireOp",EDGE,"E89.MirrorCS")}),-1.0]])]});
            var Q2;
            {var subQ4=sQuery(id+"F16.wireOp",EDGE,"E86");Q2=makeQuery(id+"F16.imprint","IMPRINT",FACE,{"disambiguationData":[TD([[makeQuery(id+"F16.imprint","IMPRINT",EDGE,{"derivedFrom":subQ4}),-1.0]])]});}
            var Q3;
            {var subQ0=sQuery(id+"F4.wireOp",EDGE,"E36.filletArc");var subQ1=sQuery(id+"F4.wireOp",EDGE,"E35.filletArc");var subQ2=sQuery(id+"F4.wireOp",EDGE,"E34.filletArc");var subQ3=sQuery(id+"F4.wireOp",EDGE,"E33.filletArc");var subQ4=sQuery(id+"F4.wireOp",EDGE,"E27.0");var subQ5=sQuery(id+"F4.wireOp",EDGE,"E30");var subQ6=sQuery(id+"F4.wireOp",EDGE,"E28.0");var subQ7=sQuery(id+"F4.wireOp",EDGE,"E29");Q3=makeQuery(id+"F6.boolean.opBoolean","SPLIT",FACE,{"disambiguationData":[TD([makeQuery(id+"F5.opExtrude","SWEPT_FACE",FACE,{"disambiguationData":[OSD([subQ4])]})])],"derivedFrom":makeQuery(id+"F5.opExtrude","CAP_FACE",FACE,{"disambiguationData":[OSD([subQ4,subQ6,subQ7,subQ5,subQ3,subQ2,subQ1,subQ0,sQuery(id+"F4.wireOp",EDGE,"E41"),sQuery(id+"F4.wireOp",EDGE,"E42"),sQuery(id+"F4.wireOp",EDGE,"E43"),sQuery(id+"F4.wireOp",EDGE,"E45"),sQuery(id+"F4.wireOp",EDGE,"E46"),sQuery(id+"F4.wireOp",EDGE,"E47.filletArc"),sQuery(id+"F4.wireOp",EDGE,"E48.filletArc"),sQuery(id+"F4.wireOp",EDGE,"E49.filletArc"),sQuery(id+"F4.wireOp",EDGE,"E50.filletArc"),sQuery(id+"F4.wireOp",EDGE,"E51.filletArc"),sQuery(id+"F4.wireOp",EDGE,"E52.filletArc"),sQuery(id+"F4.wireOp",EDGE,"E53.0.MirrorCS"),sQuery(id+"F4.wireOp",EDGE,"E54.0.MirrorCS"),sQuery(id+"F4.wireOp",EDGE,"E55.0.MirrorCS"),sQuery(id+"F4.wireOp",EDGE,"E56.0.MirrorCS"),sQuery(id+"F4.wireOp",EDGE,"E57.0.MirrorCS"),sQuery(id+"F4.wireOp",EDGE,"E58.0.MirrorCS"),sQuery(id+"F4.wireOp",EDGE,"E59.0.MirrorCS"),sQuery(id+"F4.wireOp",EDGE,"E60.0.MirrorCS"),sQuery(id+"F4.wireOp",EDGE,"E61.0.MirrorCS"),sQuery(id+"F4.wireOp",EDGE,"E62.0.MirrorCS"),sQuery(id+"F4.wireOp",EDGE,"E63.0.MirrorCS")])],"isStart":true})});}
            extrude(context, id + "F17", {"entities" : qUnion([Q0, Q1, Q2]), "endBound" : BoundingType.UP_TO_SURFACE, "depth" : 25 * mm, "endBoundEntityFace" : qUnion([Q3]), "offsetDistance" : 25 * mm});
        }
    });
